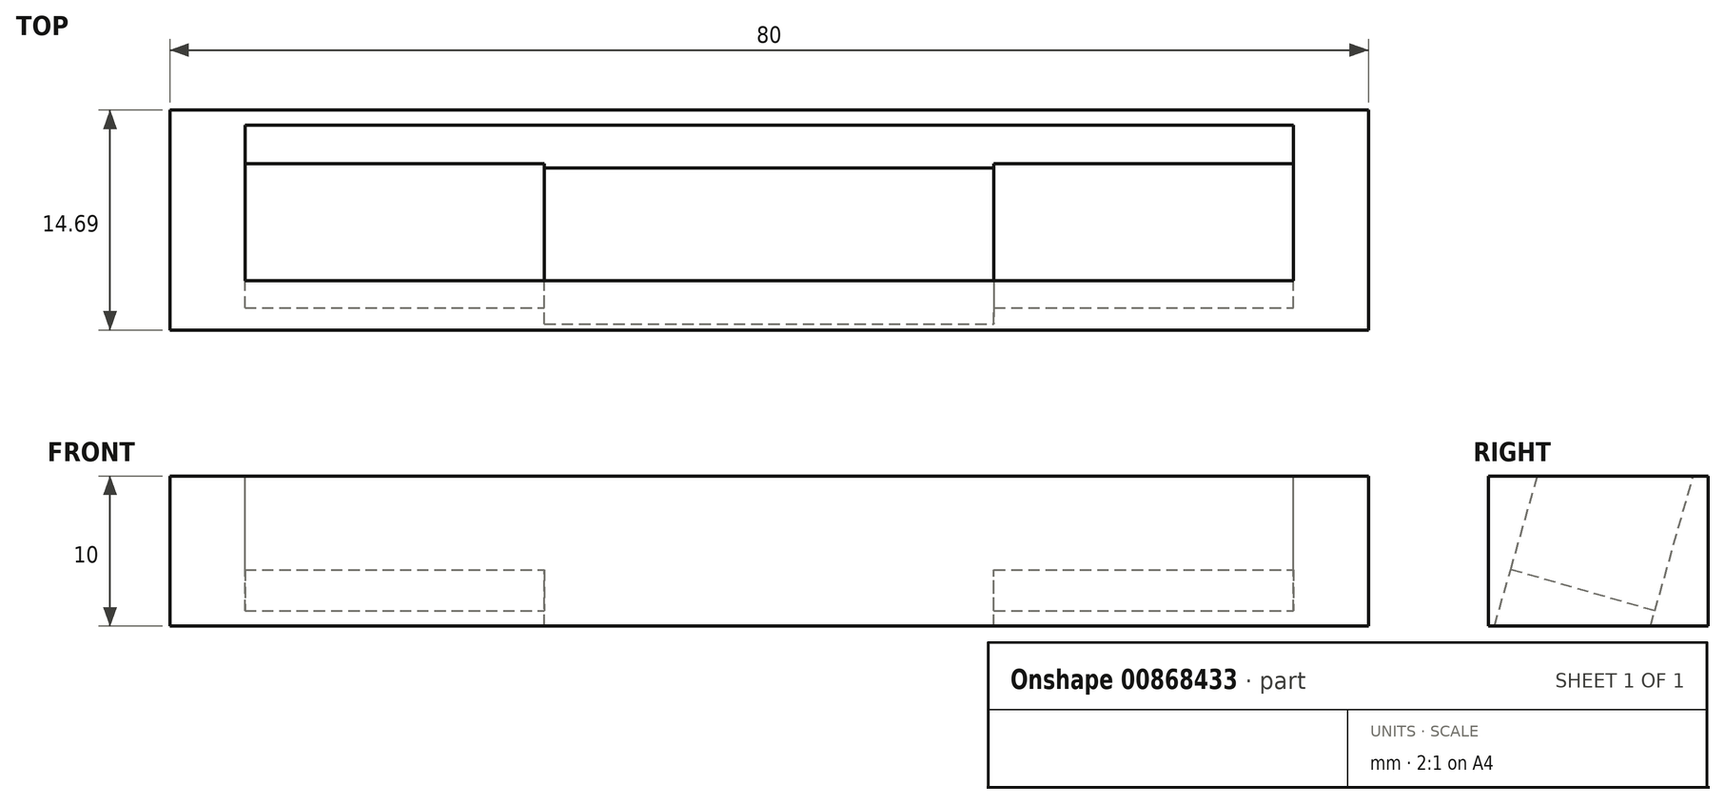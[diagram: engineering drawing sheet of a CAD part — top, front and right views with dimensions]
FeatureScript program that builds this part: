
annotation { "Feature Type Name" : "Feature", "Feature Type Description" : "" }
export const myFeature = defineFeature(function(context is Context, id is Id, definition is map)
    precondition{}
    {
        {
            var Q0;
            Q0=qCreatedBy(makeId("Right.planeOp"),FACE);
            var sketch = newSketch(context, id + "F0", { "sketchPlane" : qUnion([Q0])});
            skLineSegment(sketch, "E0.bottom", {"start": v(-5.53, 0.77) * mm, "end": v(4.08, -1.98) * mm});
            skLineSegment(sketch, "E0.left", {"start": v(-5.53, 0.77) * mm, "end": v(-3.74, 7.02) * mm});
            skLineSegment(sketch, "E0.right", {"start": v(4.08, -1.98) * mm, "end": v(6.66, 7.02) * mm});
            skLineSegment(sketch, "E1", {"start": v(6.66, 7.02) * mm, "end": v(7.66, 7.02) * mm});
            skLineSegment(sketch, "E2", {"start": v(7.66, 7.02) * mm, "end": v(6.66, 7.02) * mm});
            skLineSegment(sketch, "E3", {"start": v(7.66, 7.02) * mm, "end": v(7.66, -2.98) * mm});
            skLineSegment(sketch, "E4.trimOffspring", {"start": v(-3.74, 7.02) * mm, "end": v(-6.53, 7.02) * mm});
            skLineSegment(sketch, "E5", {"start": v(-6.53, 7.02) * mm, "end": v(-6.53, -2.98) * mm});
            skLineSegment(sketch, "E6", {"start": v(7.66, -2.98) * mm, "end": v(-6.53, -2.98) * mm});
            skSolve(sketch);
        }
        {
            var Q0;
            Q0=makeQuery(id+"F0.imprint","IMPRINT",FACE,{"disambiguationData":[TD([[makeQuery(id+"F0.imprint","IMPRINT",EDGE,{"derivedFrom":sQuery(id+"F0.wireOp",EDGE,"E0.bottom")}),-1.0]])]});
            extrude(context, id + "F1", {"entities" : qUnion([Q0]), "endBound" : BoundingType.SYMMETRIC, "oppositeDirection" : true, "depth" : 70 * mm, "offsetDistance" : 25 * mm});
        }
        {
            var Q0;
            Q0=makeQuery(id+"F1.opExtrude","SWEPT_BODY",BODY,{"disambiguationData":[OSD([sQuery(id+"F0.wireOp",EDGE,"E0.bottom"),sQuery(id+"F0.wireOp",EDGE,"E0.left"),sQuery(id+"F0.wireOp",EDGE,"E0.right"),sQuery(id+"F0.wireOp",EDGE,"E1"),sQuery(id+"F0.wireOp",EDGE,"E3"),sQuery(id+"F0.wireOp",EDGE,"E4.trimOffspring"),sQuery(id+"F0.wireOp",EDGE,"E5"),sQuery(id+"F0.wireOp",EDGE,"E6")])]});
            transform(context, id + "F2", {"entities" : qUnion([Q0]), "transformType" : TransformType.TRANSLATION_3D, "dx" : 0 * mm, "dy" : 0 * mm, "dz" : 2.98 * mm, "makeCopy" : false});
        }
        {
            var Q0;
            Q0=makeQuery(id+"F1.opExtrude","CAP_FACE",FACE,{"disambiguationData":[OSD([sQuery(id+"F0.wireOp",EDGE,"E0.bottom"),sQuery(id+"F0.wireOp",EDGE,"E0.left"),sQuery(id+"F0.wireOp",EDGE,"E0.right"),sQuery(id+"F0.wireOp",EDGE,"E1"),sQuery(id+"F0.wireOp",EDGE,"E3"),sQuery(id+"F0.wireOp",EDGE,"E4.trimOffspring"),sQuery(id+"F0.wireOp",EDGE,"E5"),sQuery(id+"F0.wireOp",EDGE,"E6")])],"isStart":false});
            var sketch = newSketch(context, id + "F3", { "sketchPlane" : qUnion([Q0])});
            skLineSegment(sketch, "E7.bottom", {"start": v(-7.66, 10) * mm, "end": v(6.53, 10) * mm});
            skLineSegment(sketch, "E7.top", {"start": v(-7.66, 0) * mm, "end": v(6.53, 0) * mm});
            skLineSegment(sketch, "E7.left", {"start": v(-7.66, 10) * mm, "end": v(-7.66, 0) * mm});
            skLineSegment(sketch, "E7.right", {"start": v(6.53, 10) * mm, "end": v(6.53, 0) * mm});
            skSolve(sketch);
        }
        {
            var Q0;
            Q0 = qSketchRegion(id + "F3", true);
            extrude(context, id + "F4", {"entities" : qUnion([Q0]), "operationType" : NewBodyOperationType.ADD, "depth" : 5 * mm, "offsetDistance" : 25 * mm});
        }
        {
            var Q0;
            Q0=makeQuery(id+"F1.opExtrude","CAP_FACE",FACE,{"disambiguationData":[OSD([sQuery(id+"F0.wireOp",EDGE,"E0.bottom"),sQuery(id+"F0.wireOp",EDGE,"E0.left"),sQuery(id+"F0.wireOp",EDGE,"E0.right"),sQuery(id+"F0.wireOp",EDGE,"E1"),sQuery(id+"F0.wireOp",EDGE,"E3"),sQuery(id+"F0.wireOp",EDGE,"E4.trimOffspring"),sQuery(id+"F0.wireOp",EDGE,"E5"),sQuery(id+"F0.wireOp",EDGE,"E6")])],"isStart":true});
            var sketch = newSketch(context, id + "F5", { "sketchPlane" : qUnion([Q0])});
            skLineSegment(sketch, "E8.bottom", {"start": v(-6.53, 10) * mm, "end": v(7.66, 10) * mm});
            skLineSegment(sketch, "E8.top", {"start": v(-6.53, 0) * mm, "end": v(7.66, 0) * mm});
            skLineSegment(sketch, "E8.left", {"start": v(-6.53, 10) * mm, "end": v(-6.53, 0) * mm});
            skLineSegment(sketch, "E8.right", {"start": v(7.66, 10) * mm, "end": v(7.66, 0) * mm});
            skSolve(sketch);
        }
        {
            var Q0;
            Q0=makeQuery(id+"F5.imprint","IMPRINT",FACE,{"disambiguationData":[TD([[makeQuery(id+"F5.imprint","IMPRINT",EDGE,{"derivedFrom":sQuery(id+"F5.wireOp",EDGE,"E8.top")}),-1.0]])]});
            var Q1;
            Q1=makeQuery(id+"F5.imprint","IMPRINT",FACE,{"disambiguationData":[TD([[makeQuery(id+"F5.imprint","IMPRINT",EDGE,{"derivedFrom":makeQuery(id+"F1.opExtrude","CAP_EDGE",EDGE,{"disambiguationData":[OSD([sQuery(id+"F0.wireOp",EDGE,"E0.bottom")])],"isStart":true})}),1.0]])]});
            extrude(context, id + "F6", {"entities" : qUnion([Q0, Q1]), "operationType" : NewBodyOperationType.ADD, "depth" : 5 * mm, "offsetDistance" : 25 * mm});
        }
        {
            var Q0;
            Q0=makeQuery(id+"F1.opExtrude","SWEPT_FACE",FACE,{"disambiguationData":[OSD([sQuery(id+"F0.wireOp",EDGE,"E0.bottom")])]});
            var sketch = newSketch(context, id + "F7", { "sketchPlane" : qUnion([Q0])});
            skLineSegment(sketch, "E9", {"start": v(0, 3.64) * mm, "end": v(15, 3.64) * mm});
            skLineSegment(sketch, "E10", {"start": v(15, 3.64) * mm, "end": v(15, -6.36) * mm});
            skLineSegment(sketch, "E11", {"start": v(15, -6.36) * mm, "end": v(-15, -6.36) * mm});
            skLineSegment(sketch, "E12", {"start": v(-15, -6.36) * mm, "end": v(-15, 3.64) * mm});
            skLineSegment(sketch, "E13", {"start": v(-15, 3.64) * mm, "end": v(0, 3.64) * mm});
            skSolve(sketch);
        }
        {
            var Q0;
            Q0=makeQuery(id+"F6.boolean.opBoolean","MERGE",FACE,{"derivedFrom":[makeQuery(id+"F4.boolean.opBoolean","MERGE",FACE,{"derivedFrom":[makeQuery(id+"F1.opExtrude","SWEPT_FACE",FACE,{"disambiguationData":[OSD([sQuery(id+"F0.wireOp",EDGE,"E5")])]}),makeQuery(id+"F4.opExtrude","SWEPT_FACE",FACE,{"disambiguationData":[OSD([sQuery(id+"F3.wireOp",EDGE,"E7.right")])]})]}),makeQuery(id+"F6.opExtrude","SWEPT_FACE",FACE,{"disambiguationData":[OSD([sQuery(id+"F5.wireOp",EDGE,"E8.left")])]})]});
            extrude(context, id + "F8", {"entities" : qUnion([Q0]), "operationType" : NewBodyOperationType.ADD, "depth" : 0.5 * mm, "offsetDistance" : 25 * mm});
        }
        {
            var Q0;
            Q0=makeQuery(id+"F7.imprint","IMPRINT",FACE,{"disambiguationData":[TD([[makeQuery(id+"F7.imprint","IMPRINT",EDGE,{"derivedFrom":sQuery(id+"F7.wireOp",EDGE,"E9")}),-1.0]])]});
            extrude(context, id + "F9", {"entities" : qUnion([Q0]), "operationType" : NewBodyOperationType.REMOVE, "oppositeDirection" : true, "depth" : 200 * mm, "offsetDistance" : 25 * mm});
        }
    });
